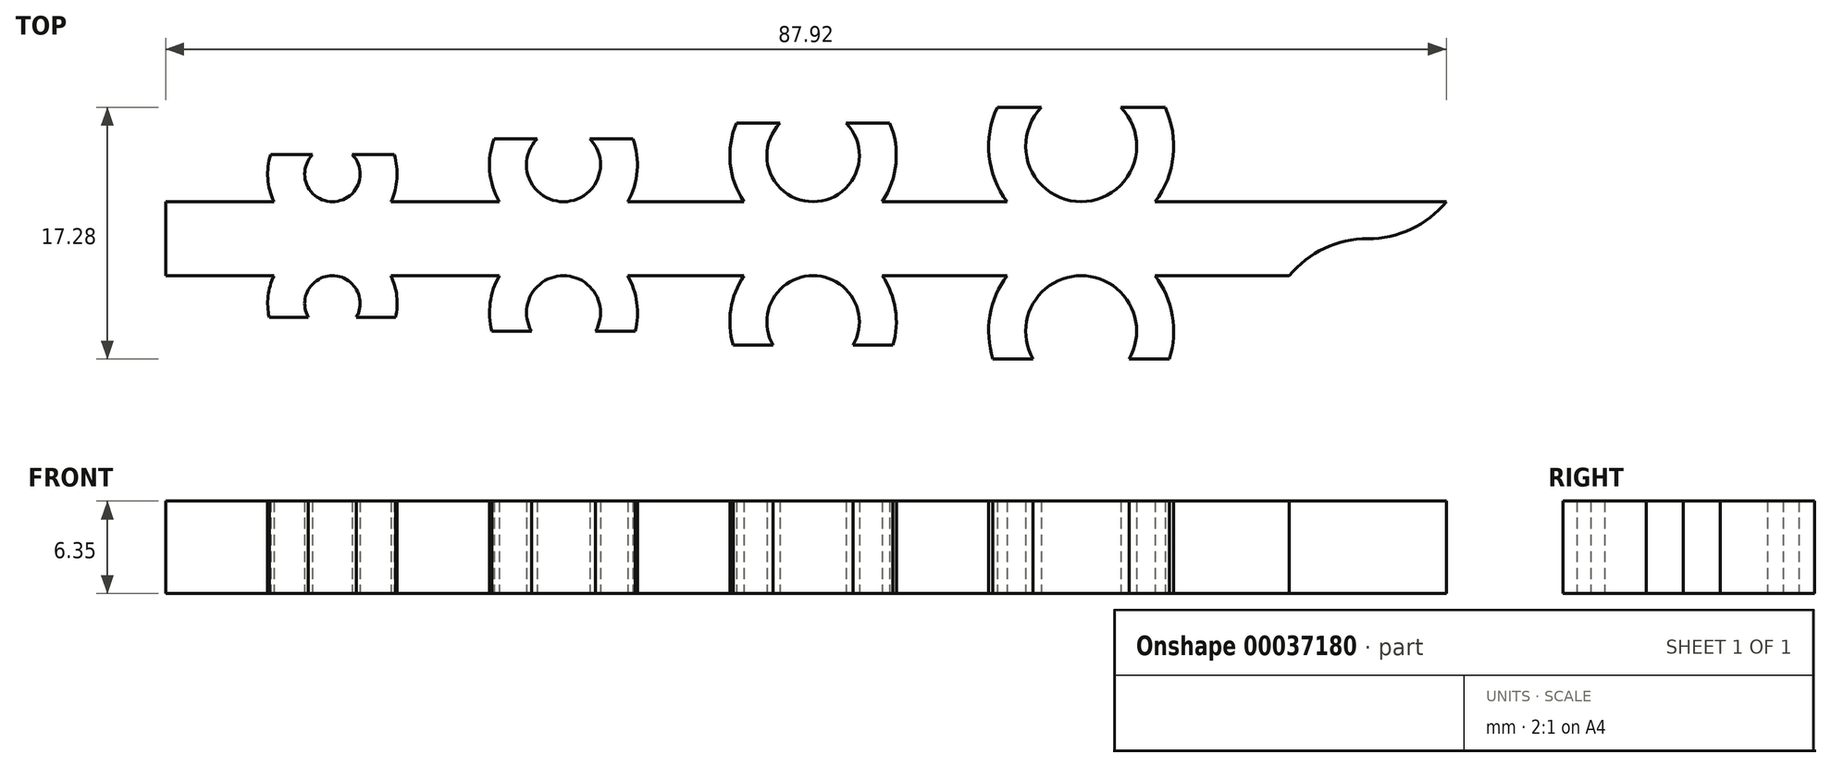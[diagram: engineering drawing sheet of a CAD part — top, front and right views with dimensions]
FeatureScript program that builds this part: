
annotation { "Feature Type Name" : "Feature", "Feature Type Description" : "" }
export const myFeature = defineFeature(function(context is Context, id is Id, definition is map)
    precondition{}
    {
        {
            var Q0;
            Q0=qCreatedBy(makeId("Top.planeOp"),FACE);
            var sketch = newSketch(context, id + "F0", { "sketchPlane" : qUnion([Q0])});
            skLineSegment(sketch, "E0.rect.bottom", {"start": v(44.45, 2.54) * mm, "end": v(-44.45, 2.54) * mm});
            skLineSegment(sketch, "E0.rect.top", {"start": v(44.45, -2.54) * mm, "end": v(-44.45, -2.54) * mm});
            skLineSegment(sketch, "E0.rect.left", {"start": v(44.45, 2.54) * mm, "end": v(44.45, -2.54) * mm});
            skLineSegment(sketch, "E0.rect.right", {"start": v(-44.45, 2.54) * mm, "end": v(-44.45, -2.54) * mm});
            skPoint(sketch, "E0.rect.middle", {"position": v(0, 0) * mm});
            skCircle(sketch, "E1", {"center": v(-33, 4.45) * mm, "radius": 1.9 * mm});
            skCircle(sketch, "E2", {"center": v(-17.13, 5.08) * mm, "radius": 2.54 * mm});
            skCircle(sketch, "E3", {"center": v(0, 5.72) * mm, "radius": 3.18 * mm});
            skCircle(sketch, "E4", {"center": v(18.4, 6.35) * mm, "radius": 3.81 * mm});
            skCircle(sketch, "E5", {"center": v(38.08, 6.99) * mm, "radius": 4.45 * mm});
            skCircle(sketch, "E6", {"center": v(-33, 4.45) * mm, "radius": 4.45 * mm});
            skCircle(sketch, "E7", {"center": v(-17.13, 5.08) * mm, "radius": 5.08 * mm});
            skCircle(sketch, "E8", {"center": v(0, 5.72) * mm, "radius": 5.72 * mm});
            skCircle(sketch, "E9", {"center": v(18.4, 6.35) * mm, "radius": 6.35 * mm});
            skCircle(sketch, "E10", {"center": v(38.08, 6.99) * mm, "radius": 6.99 * mm});
            skCircle(sketch, "E11.MirrorC", {"center": v(38.08, -6.99) * mm, "radius": 6.99 * mm});
            skCircle(sketch, "E12.MirrorC", {"center": v(18.4, -6.35) * mm, "radius": 6.35 * mm});
            skCircle(sketch, "E13.MirrorC", {"center": v(0, -5.72) * mm, "radius": 5.72 * mm});
            skLineSegment(sketch, "E14.MirrorCS", {"start": v(44.45, -2.54) * mm, "end": v(44.45, 2.54) * mm});
            skCircle(sketch, "E15.MirrorC", {"center": v(-17.13, -5.08) * mm, "radius": 5.08 * mm});
            skCircle(sketch, "E16.MirrorC", {"center": v(-33, -4.45) * mm, "radius": 4.45 * mm});
            skCircle(sketch, "E17.MirrorC", {"center": v(-33, -4.45) * mm, "radius": 1.9 * mm});
            skCircle(sketch, "E18.MirrorC", {"center": v(-17.13, -5.08) * mm, "radius": 2.54 * mm});
            skCircle(sketch, "E19.MirrorC", {"center": v(0, -5.72) * mm, "radius": 3.18 * mm});
            skCircle(sketch, "E20.MirrorC", {"center": v(38.08, -6.99) * mm, "radius": 4.45 * mm});
            skCircle(sketch, "E21.MirrorC", {"center": v(18.4, -6.35) * mm, "radius": 3.81 * mm});
            skLineSegment(sketch, "E22", {"start": v(-37.34, -5.4) * mm, "end": v(-28.65, -5.4) * mm});
            skLineSegment(sketch, "E23", {"start": v(-22.05, -6.35) * mm, "end": v(-12.21, -6.35) * mm});
            skLineSegment(sketch, "E24", {"start": v(-5.5, -7.3) * mm, "end": v(5.5, -7.3) * mm});
            skLineSegment(sketch, "E25", {"start": v(12.35, -8.26) * mm, "end": v(24.46, -8.26) * mm});
            skLineSegment(sketch, "E26", {"start": v(31.46, -9.2) * mm, "end": v(44.7, -9.2) * mm});
            skLineSegment(sketch, "E27", {"start": v(44.33, 10.1) * mm, "end": v(31.83, 10.1) * mm});
            skLineSegment(sketch, "E28", {"start": v(24.17, 9.02) * mm, "end": v(12.64, 9.02) * mm});
            skLineSegment(sketch, "E29", {"start": v(5.27, 7.94) * mm, "end": v(-5.27, 7.94) * mm});
            skLineSegment(sketch, "E30", {"start": v(-21.9, 6.86) * mm, "end": v(-12.37, 6.86) * mm});
            skLineSegment(sketch, "E31", {"start": v(-37.24, 5.78) * mm, "end": v(-28.76, 5.78) * mm});
            skLineSegment(sketch, "E32", {"start": v(41.25, 10.1) * mm, "end": v(43.07, 11.87) * mm});
            skLineSegment(sketch, "E33", {"start": v(34.9, 10.1) * mm, "end": v(33.21, 12) * mm});
            skLineSegment(sketch, "E34", {"start": v(21.12, 9.02) * mm, "end": v(23.02, 10.7) * mm});
            skLineSegment(sketch, "E35", {"start": v(15.68, 9.02) * mm, "end": v(13.8, 10.72) * mm});
            skSolve(sketch);
        }
        {
            var Q0;
            {var subQ5=sQuery(id+"F0.wireOp",EDGE,"E0.rect.right");Q0=makeQuery(id+"F0.imprint","IMPRINT",FACE,{"disambiguationData":[TD([[makeQuery(id+"F0.imprint","IMPRINT",EDGE,{"derivedFrom":subQ5}),1.0]])]});}
            var Q1;
            {var subQ3=sQuery(id+"F0.wireOp",EDGE,"E6");var subQ5=sQuery(id+"F0.wireOp",EDGE,"E0.rect.bottom");var subQ6=makeQuery(id+"F0.imprint","INTERSECT",VERTEX,{"disambiguationData":[OD(0.0)],"derivedFrom":[subQ5,subQ3]});Q1=makeQuery(id+"F0.imprint","IMPRINT",FACE,{"disambiguationData":[TD([[makeQuery(id+"F0.imprint","IMPRINT",EDGE,{"disambiguationData":[TD([[subQ6,-1.0]])],"derivedFrom":subQ5}),-1.0]])]});}
            var Q2;
            {var subQ0=sQuery(id+"F0.wireOp",EDGE,"E6");var subQ1=sQuery(id+"F0.wireOp",EDGE,"E0.rect.bottom");var subQ2=makeQuery(id+"F0.imprint","INTERSECT",VERTEX,{"disambiguationData":[OD(1.0)],"derivedFrom":[subQ1,subQ0]});Q2=makeQuery(id+"F0.imprint","IMPRINT",FACE,{"disambiguationData":[TD([[makeQuery(id+"F0.imprint","IMPRINT",EDGE,{"disambiguationData":[TD([[subQ2,1.0]])],"derivedFrom":subQ1}),-1.0]])]});}
            var Q3;
            {var subQ0=sQuery(id+"F0.wireOp",EDGE,"E6");var subQ2=sQuery(id+"F0.wireOp",EDGE,"E0.rect.bottom");var subQ3=makeQuery(id+"F0.imprint","INTERSECT",VERTEX,{"disambiguationData":[OD(0.0)],"derivedFrom":[subQ2,subQ0]});Q3=makeQuery(id+"F0.imprint","IMPRINT",FACE,{"disambiguationData":[TD([[makeQuery(id+"F0.imprint","IMPRINT",EDGE,{"disambiguationData":[TD([[subQ3,-1.0]])],"derivedFrom":subQ2}),1.0]])]});}
            var Q4;
            {var subQ0=sQuery(id+"F0.wireOp",EDGE,"E16.MirrorC");var subQ2=sQuery(id+"F0.wireOp",EDGE,"E0.rect.top");var subQ3=makeQuery(id+"F0.imprint","INTERSECT",VERTEX,{"disambiguationData":[OD(0.0)],"derivedFrom":[subQ2,subQ0]});Q4=makeQuery(id+"F0.imprint","IMPRINT",FACE,{"disambiguationData":[TD([[makeQuery(id+"F0.imprint","IMPRINT",EDGE,{"disambiguationData":[TD([[subQ3,-1.0]])],"derivedFrom":subQ2}),-1.0]])]});}
            var Q5;
            {var subQ3=sQuery(id+"F0.wireOp",EDGE,"E16.MirrorC");var subQ5=sQuery(id+"F0.wireOp",EDGE,"E0.rect.top");var subQ7=makeQuery(id+"F0.imprint","INTERSECT",VERTEX,{"disambiguationData":[OD(1.0)],"derivedFrom":[subQ5,subQ3]});Q5=makeQuery(id+"F0.imprint","IMPRINT",FACE,{"disambiguationData":[TD([[makeQuery(id+"F0.imprint","IMPRINT",EDGE,{"disambiguationData":[TD([[subQ7,1.0]])],"derivedFrom":subQ5}),1.0]])]});}
            var Q6;
            {var subQ3=sQuery(id+"F0.wireOp",EDGE,"E16.MirrorC");var subQ5=sQuery(id+"F0.wireOp",EDGE,"E0.rect.top");var subQ7=makeQuery(id+"F0.imprint","INTERSECT",VERTEX,{"disambiguationData":[OD(0.0)],"derivedFrom":[subQ5,subQ3]});Q6=makeQuery(id+"F0.imprint","IMPRINT",FACE,{"disambiguationData":[TD([[makeQuery(id+"F0.imprint","IMPRINT",EDGE,{"disambiguationData":[TD([[subQ7,-1.0]])],"derivedFrom":subQ5}),1.0]])]});}
            var Q7;
            {var subQ6=sQuery(id+"F0.wireOp",EDGE,"E7");var subQ9=sQuery(id+"F0.wireOp",EDGE,"E0.rect.bottom");var subQ10=makeQuery(id+"F0.imprint","INTERSECT",VERTEX,{"disambiguationData":[OD(1.0)],"derivedFrom":[subQ9,subQ6]});Q7=makeQuery(id+"F0.imprint","IMPRINT",FACE,{"disambiguationData":[TD([[makeQuery(id+"F0.imprint","IMPRINT",EDGE,{"disambiguationData":[TD([[subQ10,-1.0]])],"derivedFrom":subQ9}),1.0]])]});}
            var Q8;
            {var subQ3=sQuery(id+"F0.wireOp",EDGE,"E15.MirrorC");var subQ5=sQuery(id+"F0.wireOp",EDGE,"E0.rect.top");var subQ7=makeQuery(id+"F0.imprint","INTERSECT",VERTEX,{"disambiguationData":[OD(1.0)],"derivedFrom":[subQ5,subQ3]});Q8=makeQuery(id+"F0.imprint","IMPRINT",FACE,{"disambiguationData":[TD([[makeQuery(id+"F0.imprint","IMPRINT",EDGE,{"disambiguationData":[TD([[subQ7,1.0]])],"derivedFrom":subQ5}),1.0]])]});}
            var Q9;
            {var subQ3=sQuery(id+"F0.wireOp",EDGE,"E15.MirrorC");var subQ5=sQuery(id+"F0.wireOp",EDGE,"E0.rect.top");var subQ7=makeQuery(id+"F0.imprint","INTERSECT",VERTEX,{"disambiguationData":[OD(0.0)],"derivedFrom":[subQ5,subQ3]});Q9=makeQuery(id+"F0.imprint","IMPRINT",FACE,{"disambiguationData":[TD([[makeQuery(id+"F0.imprint","IMPRINT",EDGE,{"disambiguationData":[TD([[subQ7,-1.0]])],"derivedFrom":subQ5}),1.0]])]});}
            var Q10;
            {var subQ0=sQuery(id+"F0.wireOp",EDGE,"E15.MirrorC");var subQ2=sQuery(id+"F0.wireOp",EDGE,"E0.rect.top");var subQ3=makeQuery(id+"F0.imprint","INTERSECT",VERTEX,{"disambiguationData":[OD(0.0)],"derivedFrom":[subQ2,subQ0]});Q10=makeQuery(id+"F0.imprint","IMPRINT",FACE,{"disambiguationData":[TD([[makeQuery(id+"F0.imprint","IMPRINT",EDGE,{"disambiguationData":[TD([[subQ3,-1.0]])],"derivedFrom":subQ2}),-1.0]])]});}
            var Q11;
            {var subQ3=sQuery(id+"F0.wireOp",EDGE,"E7");var subQ5=sQuery(id+"F0.wireOp",EDGE,"E0.rect.bottom");var subQ6=makeQuery(id+"F0.imprint","INTERSECT",VERTEX,{"disambiguationData":[OD(1.0)],"derivedFrom":[subQ5,subQ3]});Q11=makeQuery(id+"F0.imprint","IMPRINT",FACE,{"disambiguationData":[TD([[makeQuery(id+"F0.imprint","IMPRINT",EDGE,{"disambiguationData":[TD([[subQ6,1.0]])],"derivedFrom":subQ5}),-1.0]])]});}
            var Q12;
            {var subQ0=sQuery(id+"F0.wireOp",EDGE,"E7");var subQ2=sQuery(id+"F0.wireOp",EDGE,"E0.rect.bottom");var subQ3=makeQuery(id+"F0.imprint","INTERSECT",VERTEX,{"disambiguationData":[OD(0.0)],"derivedFrom":[subQ2,subQ0]});Q12=makeQuery(id+"F0.imprint","IMPRINT",FACE,{"disambiguationData":[TD([[makeQuery(id+"F0.imprint","IMPRINT",EDGE,{"disambiguationData":[TD([[subQ3,-1.0]])],"derivedFrom":subQ2}),1.0]])]});}
            var Q13;
            {var subQ0=sQuery(id+"F0.wireOp",EDGE,"E7");var subQ1=sQuery(id+"F0.wireOp",EDGE,"E0.rect.bottom");var subQ2=makeQuery(id+"F0.imprint","INTERSECT",VERTEX,{"disambiguationData":[OD(0.0)],"derivedFrom":[subQ1,subQ0]});Q13=makeQuery(id+"F0.imprint","IMPRINT",FACE,{"disambiguationData":[TD([[makeQuery(id+"F0.imprint","IMPRINT",EDGE,{"disambiguationData":[TD([[subQ2,-1.0]])],"derivedFrom":subQ1}),-1.0]])]});}
            var Q14;
            {var subQ7=sQuery(id+"F0.wireOp",EDGE,"E8");var subQ9=sQuery(id+"F0.wireOp",EDGE,"E0.rect.bottom");var subQ10=makeQuery(id+"F0.imprint","INTERSECT",VERTEX,{"disambiguationData":[OD(1.0)],"derivedFrom":[subQ9,subQ7]});Q14=makeQuery(id+"F0.imprint","IMPRINT",FACE,{"disambiguationData":[TD([[makeQuery(id+"F0.imprint","IMPRINT",EDGE,{"disambiguationData":[TD([[subQ10,-1.0]])],"derivedFrom":subQ9}),1.0]])]});}
            var Q15;
            {var subQ3=sQuery(id+"F0.wireOp",EDGE,"E8");var subQ5=sQuery(id+"F0.wireOp",EDGE,"E0.rect.bottom");var subQ6=makeQuery(id+"F0.imprint","INTERSECT",VERTEX,{"disambiguationData":[OD(1.0)],"derivedFrom":[subQ5,subQ3]});Q15=makeQuery(id+"F0.imprint","IMPRINT",FACE,{"disambiguationData":[TD([[makeQuery(id+"F0.imprint","IMPRINT",EDGE,{"disambiguationData":[TD([[subQ6,1.0]])],"derivedFrom":subQ5}),-1.0]])]});}
            var Q16;
            {var subQ0=sQuery(id+"F0.wireOp",EDGE,"E8");var subQ2=sQuery(id+"F0.wireOp",EDGE,"E0.rect.bottom");var subQ3=makeQuery(id+"F0.imprint","INTERSECT",VERTEX,{"disambiguationData":[OD(0.0)],"derivedFrom":[subQ2,subQ0]});Q16=makeQuery(id+"F0.imprint","IMPRINT",FACE,{"disambiguationData":[TD([[makeQuery(id+"F0.imprint","IMPRINT",EDGE,{"disambiguationData":[TD([[subQ3,-1.0]])],"derivedFrom":subQ2}),1.0]])]});}
            var Q17;
            {var subQ3=sQuery(id+"F0.wireOp",EDGE,"E8");var subQ5=sQuery(id+"F0.wireOp",EDGE,"E0.rect.bottom");var subQ6=makeQuery(id+"F0.imprint","INTERSECT",VERTEX,{"disambiguationData":[OD(0.0)],"derivedFrom":[subQ5,subQ3]});Q17=makeQuery(id+"F0.imprint","IMPRINT",FACE,{"disambiguationData":[TD([[makeQuery(id+"F0.imprint","IMPRINT",EDGE,{"disambiguationData":[TD([[subQ6,-1.0]])],"derivedFrom":subQ5}),-1.0]])]});}
            var Q18;
            {var subQ3=sQuery(id+"F0.wireOp",EDGE,"E13.MirrorC");var subQ5=sQuery(id+"F0.wireOp",EDGE,"E0.rect.top");var subQ6=makeQuery(id+"F0.imprint","INTERSECT",VERTEX,{"disambiguationData":[OD(1.0)],"derivedFrom":[subQ5,subQ3]});Q18=makeQuery(id+"F0.imprint","IMPRINT",FACE,{"disambiguationData":[TD([[makeQuery(id+"F0.imprint","IMPRINT",EDGE,{"disambiguationData":[TD([[subQ6,1.0]])],"derivedFrom":subQ5}),1.0]])]});}
            var Q19;
            {var subQ0=sQuery(id+"F0.wireOp",EDGE,"E13.MirrorC");var subQ2=sQuery(id+"F0.wireOp",EDGE,"E0.rect.top");var subQ3=makeQuery(id+"F0.imprint","INTERSECT",VERTEX,{"disambiguationData":[OD(0.0)],"derivedFrom":[subQ2,subQ0]});Q19=makeQuery(id+"F0.imprint","IMPRINT",FACE,{"disambiguationData":[TD([[makeQuery(id+"F0.imprint","IMPRINT",EDGE,{"disambiguationData":[TD([[subQ3,-1.0]])],"derivedFrom":subQ2}),-1.0]])]});}
            var Q20;
            {var subQ3=sQuery(id+"F0.wireOp",EDGE,"E13.MirrorC");var subQ5=sQuery(id+"F0.wireOp",EDGE,"E0.rect.top");var subQ7=makeQuery(id+"F0.imprint","INTERSECT",VERTEX,{"disambiguationData":[OD(0.0)],"derivedFrom":[subQ5,subQ3]});Q20=makeQuery(id+"F0.imprint","IMPRINT",FACE,{"disambiguationData":[TD([[makeQuery(id+"F0.imprint","IMPRINT",EDGE,{"disambiguationData":[TD([[subQ7,-1.0]])],"derivedFrom":subQ5}),1.0]])]});}
            var Q21;
            {var subQ3=sQuery(id+"F0.wireOp",EDGE,"E9");var subQ5=sQuery(id+"F0.wireOp",EDGE,"E0.rect.bottom");var subQ7=makeQuery(id+"F0.imprint","INTERSECT",VERTEX,{"disambiguationData":[OD(1.0)],"derivedFrom":[subQ5,subQ3]});Q21=makeQuery(id+"F0.imprint","IMPRINT",FACE,{"disambiguationData":[TD([[makeQuery(id+"F0.imprint","IMPRINT",EDGE,{"disambiguationData":[TD([[subQ7,1.0]])],"derivedFrom":subQ5}),-1.0]])]});}
            var Q22;
            {var subQ0=sQuery(id+"F0.wireOp",EDGE,"E9");var subQ2=sQuery(id+"F0.wireOp",EDGE,"E0.rect.bottom");var subQ3=makeQuery(id+"F0.imprint","INTERSECT",VERTEX,{"disambiguationData":[OD(0.0)],"derivedFrom":[subQ2,subQ0]});Q22=makeQuery(id+"F0.imprint","IMPRINT",FACE,{"disambiguationData":[TD([[makeQuery(id+"F0.imprint","IMPRINT",EDGE,{"disambiguationData":[TD([[subQ3,-1.0]])],"derivedFrom":subQ2}),1.0]])]});}
            var Q23;
            {var subQ3=sQuery(id+"F0.wireOp",EDGE,"E9");var subQ5=sQuery(id+"F0.wireOp",EDGE,"E0.rect.bottom");var subQ6=makeQuery(id+"F0.imprint","INTERSECT",VERTEX,{"disambiguationData":[OD(0.0)],"derivedFrom":[subQ5,subQ3]});Q23=makeQuery(id+"F0.imprint","IMPRINT",FACE,{"disambiguationData":[TD([[makeQuery(id+"F0.imprint","IMPRINT",EDGE,{"disambiguationData":[TD([[subQ6,-1.0]])],"derivedFrom":subQ5}),-1.0]])]});}
            var Q24;
            {var subQ3=sQuery(id+"F0.wireOp",EDGE,"E12.MirrorC");var subQ5=sQuery(id+"F0.wireOp",EDGE,"E0.rect.top");var subQ7=makeQuery(id+"F0.imprint","INTERSECT",VERTEX,{"disambiguationData":[OD(1.0)],"derivedFrom":[subQ5,subQ3]});Q24=makeQuery(id+"F0.imprint","IMPRINT",FACE,{"disambiguationData":[TD([[makeQuery(id+"F0.imprint","IMPRINT",EDGE,{"disambiguationData":[TD([[subQ7,1.0]])],"derivedFrom":subQ5}),1.0]])]});}
            var Q25;
            {var subQ0=sQuery(id+"F0.wireOp",EDGE,"E12.MirrorC");var subQ2=sQuery(id+"F0.wireOp",EDGE,"E0.rect.top");var subQ3=makeQuery(id+"F0.imprint","INTERSECT",VERTEX,{"disambiguationData":[OD(0.0)],"derivedFrom":[subQ2,subQ0]});Q25=makeQuery(id+"F0.imprint","IMPRINT",FACE,{"disambiguationData":[TD([[makeQuery(id+"F0.imprint","IMPRINT",EDGE,{"disambiguationData":[TD([[subQ3,-1.0]])],"derivedFrom":subQ2}),-1.0]])]});}
            var Q26;
            {var subQ3=sQuery(id+"F0.wireOp",EDGE,"E12.MirrorC");var subQ5=sQuery(id+"F0.wireOp",EDGE,"E0.rect.top");var subQ6=makeQuery(id+"F0.imprint","INTERSECT",VERTEX,{"disambiguationData":[OD(0.0)],"derivedFrom":[subQ5,subQ3]});Q26=makeQuery(id+"F0.imprint","IMPRINT",FACE,{"disambiguationData":[TD([[makeQuery(id+"F0.imprint","IMPRINT",EDGE,{"disambiguationData":[TD([[subQ6,-1.0]])],"derivedFrom":subQ5}),1.0]])]});}
            var Q27;
            {var subQ6=sQuery(id+"F0.wireOp",EDGE,"E10");var subQ9=sQuery(id+"F0.wireOp",EDGE,"E0.rect.bottom");var subQ10=makeQuery(id+"F0.imprint","INTERSECT",VERTEX,{"disambiguationData":[OD(1.0)],"derivedFrom":[subQ9,subQ6]});Q27=makeQuery(id+"F0.imprint","IMPRINT",FACE,{"disambiguationData":[TD([[makeQuery(id+"F0.imprint","IMPRINT",EDGE,{"disambiguationData":[TD([[subQ10,-1.0]])],"derivedFrom":subQ9}),1.0]])]});}
            var Q28;
            {var subQ3=sQuery(id+"F0.wireOp",EDGE,"E10");var subQ5=sQuery(id+"F0.wireOp",EDGE,"E0.rect.bottom");var subQ6=makeQuery(id+"F0.imprint","INTERSECT",VERTEX,{"disambiguationData":[OD(1.0)],"derivedFrom":[subQ5,subQ3]});Q28=makeQuery(id+"F0.imprint","IMPRINT",FACE,{"disambiguationData":[TD([[makeQuery(id+"F0.imprint","IMPRINT",EDGE,{"disambiguationData":[TD([[subQ6,1.0]])],"derivedFrom":subQ5}),-1.0]])]});}
            var Q29;
            {var subQ0=sQuery(id+"F0.wireOp",EDGE,"E10");var subQ2=sQuery(id+"F0.wireOp",EDGE,"E0.rect.bottom");var subQ3=makeQuery(id+"F0.imprint","INTERSECT",VERTEX,{"disambiguationData":[OD(0.0)],"derivedFrom":[subQ2,subQ0]});Q29=makeQuery(id+"F0.imprint","IMPRINT",FACE,{"disambiguationData":[TD([[makeQuery(id+"F0.imprint","IMPRINT",EDGE,{"disambiguationData":[TD([[subQ3,-1.0]])],"derivedFrom":subQ2}),1.0]])]});}
            var Q30;
            {var subQ3=sQuery(id+"F0.wireOp",EDGE,"E10");var subQ5=sQuery(id+"F0.wireOp",EDGE,"E0.rect.bottom");var subQ6=makeQuery(id+"F0.imprint","INTERSECT",VERTEX,{"disambiguationData":[OD(0.0)],"derivedFrom":[subQ5,subQ3]});Q30=makeQuery(id+"F0.imprint","IMPRINT",FACE,{"disambiguationData":[TD([[makeQuery(id+"F0.imprint","IMPRINT",EDGE,{"disambiguationData":[TD([[subQ6,-1.0]])],"derivedFrom":subQ5}),-1.0]])]});}
            var Q31;
            {var subQ0=sQuery(id+"F0.wireOp",EDGE,"E11.MirrorC");var subQ2=sQuery(id+"F0.wireOp",EDGE,"E0.rect.top");var subQ3=makeQuery(id+"F0.imprint","INTERSECT",VERTEX,{"disambiguationData":[OD(0.0)],"derivedFrom":[subQ2,subQ0]});Q31=makeQuery(id+"F0.imprint","IMPRINT",FACE,{"disambiguationData":[TD([[makeQuery(id+"F0.imprint","IMPRINT",EDGE,{"disambiguationData":[TD([[subQ3,-1.0]])],"derivedFrom":subQ2}),-1.0]])]});}
            var Q32;
            {var subQ3=sQuery(id+"F0.wireOp",EDGE,"E11.MirrorC");var subQ5=sQuery(id+"F0.wireOp",EDGE,"E0.rect.top");var subQ7=makeQuery(id+"F0.imprint","INTERSECT",VERTEX,{"disambiguationData":[OD(1.0)],"derivedFrom":[subQ5,subQ3]});Q32=makeQuery(id+"F0.imprint","IMPRINT",FACE,{"disambiguationData":[TD([[makeQuery(id+"F0.imprint","IMPRINT",EDGE,{"disambiguationData":[TD([[subQ7,1.0]])],"derivedFrom":subQ5}),1.0]])]});}
            var Q33;
            {var subQ3=sQuery(id+"F0.wireOp",EDGE,"E11.MirrorC");var subQ5=sQuery(id+"F0.wireOp",EDGE,"E0.rect.top");var subQ7=makeQuery(id+"F0.imprint","INTERSECT",VERTEX,{"disambiguationData":[OD(0.0)],"derivedFrom":[subQ5,subQ3]});Q33=makeQuery(id+"F0.imprint","IMPRINT",FACE,{"disambiguationData":[TD([[makeQuery(id+"F0.imprint","IMPRINT",EDGE,{"disambiguationData":[TD([[subQ7,-1.0]])],"derivedFrom":subQ5}),1.0]])]});}
            var Q34;
            {var subQ0=sQuery(id+"F0.wireOp",EDGE,"E14.MirrorCS");Q34=makeQuery(id+"F0.imprint","IMPRINT",FACE,{"disambiguationData":[TD([[makeQuery(id+"F0.imprint","IMPRINT",EDGE,{"derivedFrom":subQ0}),1.0]])]});}
            var Q35;
            {var subQ1=sQuery(id+"F0.wireOp",EDGE,"E9");var subQ7=sQuery(id+"F0.wireOp",EDGE,"E0.rect.bottom");var subQ8=makeQuery(id+"F0.imprint","INTERSECT",VERTEX,{"disambiguationData":[OD(1.0)],"derivedFrom":[subQ7,subQ1]});Q35=makeQuery(id+"F0.imprint","IMPRINT",FACE,{"disambiguationData":[TD([[makeQuery(id+"F0.imprint","IMPRINT",EDGE,{"disambiguationData":[TD([[subQ8,-1.0]])],"derivedFrom":subQ7}),1.0]])]});}
            extrude(context, id + "F1", {"entities" : qUnion([Q0, Q1, Q2, Q3, Q4, Q5, Q6, Q7, Q8, Q9, Q10, Q11, Q12, Q13, Q14, Q15, Q16, Q17, Q18, Q19, Q20, Q21, Q22, Q23, Q24, Q25, Q26, Q27, Q28, Q29, Q30, Q31, Q32, Q33, Q34, Q35]), "depth" : 6.35 * mm});
        }
    });
